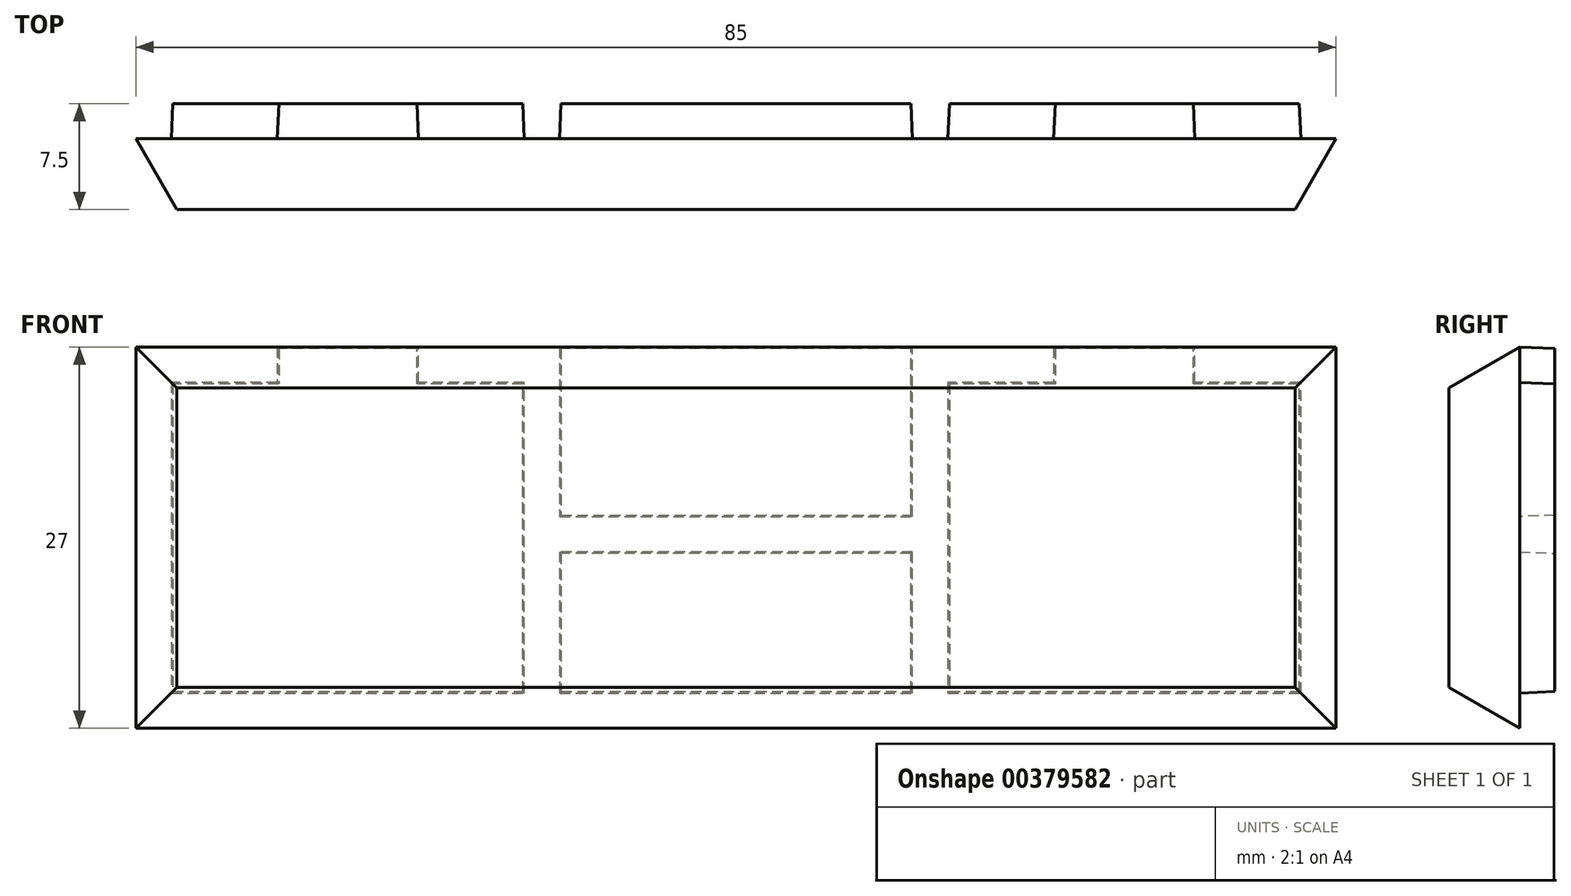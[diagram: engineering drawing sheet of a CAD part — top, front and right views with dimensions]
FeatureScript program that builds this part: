
annotation { "Feature Type Name" : "Feature", "Feature Type Description" : "" }
export const myFeature = defineFeature(function(context is Context, id is Id, definition is map)
    precondition{}
    {
        {
            var Q0;
            Q0=qCreatedBy(makeId("Front.planeOp"),FACE);
            var sketch = newSketch(context, id + "F0", { "sketchPlane" : qUnion([Q0])});
            skLineSegment(sketch, "E0.bottom", {"start": v(42.5, 17.5) * mm, "end": v(-42.5, 17.5) * mm});
            skLineSegment(sketch, "E0.top", {"start": v(42.5, -17.5) * mm, "end": v(-42.5, -17.5) * mm});
            skLineSegment(sketch, "E0.left", {"start": v(42.5, 17.5) * mm, "end": v(42.5, -17.5) * mm});
            skLineSegment(sketch, "E0.right", {"start": v(-42.5, 17.5) * mm, "end": v(-42.5, -17.5) * mm});
            skPoint(sketch, "E0.middle", {"position": v(0, 0) * mm});
            skLineSegment(sketch, "E1.bottom", {"start": v(-15, 7) * mm, "end": v(-40, 7) * mm});
            skLineSegment(sketch, "E1.top", {"start": v(-15, -15) * mm, "end": v(-40, -15) * mm});
            skLineSegment(sketch, "E1.left", {"start": v(-15, 7) * mm, "end": v(-15, -15) * mm});
            skLineSegment(sketch, "E1.right", {"start": v(-40, 7) * mm, "end": v(-40, -15) * mm});
            skPoint(sketch, "E1.middle", {"position": v(-27.5, -4) * mm});
            skLineSegment(sketch, "E2.MirrorCS", {"start": v(15, 7) * mm, "end": v(40, 7) * mm});
            skLineSegment(sketch, "E3.MirrorCS", {"start": v(15, 7) * mm, "end": v(15, -15) * mm});
            skLineSegment(sketch, "E4.MirrorCS", {"start": v(15, -15) * mm, "end": v(40, -15) * mm});
            skLineSegment(sketch, "E5.MirrorCS", {"start": v(40, 7) * mm, "end": v(40, -15) * mm});
            skLineSegment(sketch, "E6.bottom", {"start": v(12.5, -5) * mm, "end": v(-12.5, -5) * mm});
            skLineSegment(sketch, "E6.top", {"start": v(12.5, -15) * mm, "end": v(-12.5, -15) * mm});
            skLineSegment(sketch, "E6.left", {"start": v(12.5, -5) * mm, "end": v(12.5, -15) * mm});
            skLineSegment(sketch, "E6.right", {"start": v(-12.5, -5) * mm, "end": v(-12.5, -15) * mm});
            skPoint(sketch, "E6.middle", {"position": v(0, -10) * mm});
            skLineSegment(sketch, "E7.bottom", {"start": v(12.5, 17.5) * mm, "end": v(-12.5, 17.5) * mm});
            skLineSegment(sketch, "E7.top", {"start": v(12.5, -2.5) * mm, "end": v(-12.5, -2.5) * mm});
            skLineSegment(sketch, "E7.left", {"start": v(12.5, 17.5) * mm, "end": v(12.5, -2.5) * mm});
            skLineSegment(sketch, "E7.right", {"start": v(-12.5, 17.5) * mm, "end": v(-12.5, -2.5) * mm});
            skPoint(sketch, "E7.middle", {"position": v(0, 7.5) * mm});
            skLineSegment(sketch, "E8", {"start": v(-42.5, 9.5) * mm, "end": v(-32.5, 9.5) * mm});
            skLineSegment(sketch, "E9", {"start": v(-32.5, 9.5) * mm, "end": v(-32.5, 7) * mm});
            skLineSegment(sketch, "E10", {"start": v(-12.5, 9.5) * mm, "end": v(-22.5, 9.5) * mm});
            skLineSegment(sketch, "E11", {"start": v(-22.5, 9.5) * mm, "end": v(-22.5, 7) * mm});
            skLineSegment(sketch, "E12.MirrorCS", {"start": v(12.5, 9.5) * mm, "end": v(22.5, 9.5) * mm});
            skLineSegment(sketch, "E13.MirrorCS", {"start": v(22.5, 9.5) * mm, "end": v(22.5, 7) * mm});
            skLineSegment(sketch, "E14.MirrorCS", {"start": v(32.5, 9.5) * mm, "end": v(32.5, 7) * mm});
            skLineSegment(sketch, "E15.MirrorCS", {"start": v(42.5, 9.5) * mm, "end": v(32.5, 9.5) * mm});
            skLineSegment(sketch, "E16", {"start": v(-32.5, 9.5) * mm, "end": v(-22.5, 9.5) * mm});
            skLineSegment(sketch, "E17.MirrorCS", {"start": v(32.5, 9.5) * mm, "end": v(22.5, 9.5) * mm});
            skLineSegment(sketch, "E18", {"start": v(-12.5, 9.5) * mm, "end": v(12.5, 9.5) * mm});
            skSolve(sketch);
        }
        {
            var Q0;
            {var subQ10=sQuery(id+"F0.wireOp",EDGE,"E0.top");Q0=makeQuery(id+"F0.imprint","IMPRINT",FACE,{"disambiguationData":[TD([[makeQuery(id+"F0.imprint","IMPRINT",EDGE,{"derivedFrom":subQ10}),-1.0]])]});}
            var Q1;
            {var subQ0=sQuery(id+"F0.wireOp",EDGE,"E13.MirrorCS");Q1=makeQuery(id+"F0.imprint","IMPRINT",FACE,{"disambiguationData":[TD([[makeQuery(id+"F0.imprint","IMPRINT",EDGE,{"derivedFrom":subQ0}),1.0]])]});}
            var Q2;
            {var subQ0=sQuery(id+"F0.wireOp",EDGE,"E3.MirrorCS");Q2=makeQuery(id+"F0.imprint","IMPRINT",FACE,{"disambiguationData":[TD([[makeQuery(id+"F0.imprint","IMPRINT",EDGE,{"derivedFrom":subQ0}),1.0]])]});}
            var Q3;
            {var subQ0=sQuery(id+"F0.wireOp",EDGE,"E7.top");Q3=makeQuery(id+"F0.imprint","IMPRINT",FACE,{"disambiguationData":[TD([[makeQuery(id+"F0.imprint","IMPRINT",EDGE,{"derivedFrom":subQ0}),-1.0]])]});}
            var Q4;
            Q4=makeQuery(id+"F0.imprint","IMPRINT",FACE,{"disambiguationData":[TD([[makeQuery(id+"F0.imprint","IMPRINT",EDGE,{"derivedFrom":sQuery(id+"F0.wireOp",EDGE,"E6.bottom")}),1.0]])]});
            var Q5;
            Q5=makeQuery(id+"F0.imprint","IMPRINT",FACE,{"disambiguationData":[TD([[makeQuery(id+"F0.imprint","IMPRINT",EDGE,{"derivedFrom":sQuery(id+"F0.wireOp",EDGE,"E1.top")}),-1.0]])]});
            var Q6;
            {var subQ0=sQuery(id+"F0.wireOp",EDGE,"E9");Q6=makeQuery(id+"F0.imprint","IMPRINT",FACE,{"disambiguationData":[TD([[makeQuery(id+"F0.imprint","IMPRINT",EDGE,{"derivedFrom":subQ0}),1.0]])]});}
            extrude(context, id + "F1", {"entities" : qUnion([Q0, Q1, Q2, Q3, Q4, Q5, Q6]), "depth" : 5 * mm, "hasDraft" : true, "draftAngle" : 30 * degree, "draftPullDirection" : true});
        }
        {
            var Q0;
            {var subQ0=sQuery(id+"F0.wireOp",EDGE,"E3.MirrorCS");Q0=makeQuery(id+"F0.imprint","IMPRINT",FACE,{"disambiguationData":[TD([[makeQuery(id+"F0.imprint","IMPRINT",EDGE,{"derivedFrom":subQ0}),1.0]])]});}
            var Q1;
            Q1=makeQuery(id+"F0.imprint","IMPRINT",FACE,{"disambiguationData":[TD([[makeQuery(id+"F0.imprint","IMPRINT",EDGE,{"derivedFrom":sQuery(id+"F0.wireOp",EDGE,"E1.top")}),-1.0]])]});
            var Q2;
            Q2=makeQuery(id+"F0.imprint","IMPRINT",FACE,{"disambiguationData":[TD([[makeQuery(id+"F0.imprint","IMPRINT",EDGE,{"derivedFrom":sQuery(id+"F0.wireOp",EDGE,"E6.bottom")}),1.0]])]});
            var Q3;
            {var subQ0=sQuery(id+"F0.wireOp",EDGE,"E7.top");Q3=makeQuery(id+"F0.imprint","IMPRINT",FACE,{"disambiguationData":[TD([[makeQuery(id+"F0.imprint","IMPRINT",EDGE,{"derivedFrom":subQ0}),-1.0]])]});}
            var Q4;
            {var subQ0=sQuery(id+"F0.wireOp",EDGE,"E13.MirrorCS");Q4=makeQuery(id+"F0.imprint","IMPRINT",FACE,{"disambiguationData":[TD([[makeQuery(id+"F0.imprint","IMPRINT",EDGE,{"derivedFrom":subQ0}),1.0]])]});}
            var Q5;
            {var subQ0=sQuery(id+"F0.wireOp",EDGE,"E9");Q5=makeQuery(id+"F0.imprint","IMPRINT",FACE,{"disambiguationData":[TD([[makeQuery(id+"F0.imprint","IMPRINT",EDGE,{"derivedFrom":subQ0}),1.0]])]});}
            extrude(context, id + "F2", {"entities" : qUnion([Q0, Q1, Q2, Q3, Q4, Q5]), "operationType" : NewBodyOperationType.ADD, "oppositeDirection" : true, "depth" : 2.5 * mm, "hasDraft" : true, "draftAngle" : 2.5 * degree, "draftPullDirection" : true});
        }
    });
